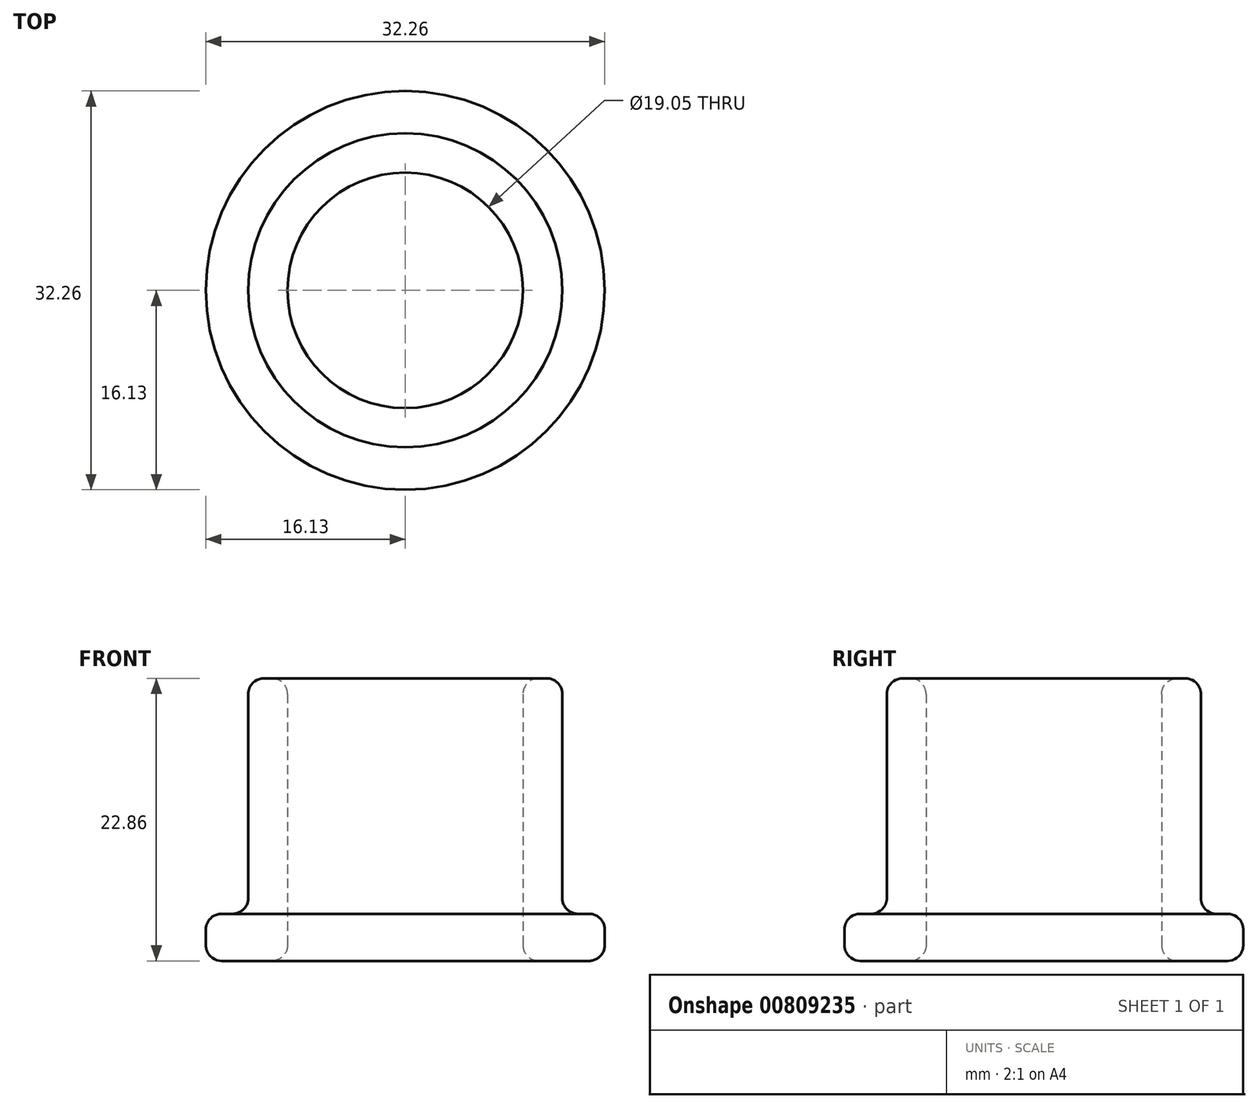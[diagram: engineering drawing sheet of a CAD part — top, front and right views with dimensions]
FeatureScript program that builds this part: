
annotation { "Feature Type Name" : "Feature", "Feature Type Description" : "" }
export const myFeature = defineFeature(function(context is Context, id is Id, definition is map)
    precondition{}
    {
        {
            var Q0;
            Q0=qCreatedBy(makeId("Front.planeOp"),FACE);
            var sketch = newSketch(context, id + "F0", { "sketchPlane" : qUnion([Q0])});
            skLineSegment(sketch, "E0", {"start": v(0, 0) * mm, "end": v(0, 26.62) * mm, "construction": true});
            skLineSegment(sketch, "E1", {"start": v(0, 0) * mm, "end": v(-16.13, 0) * mm, "construction": true});
            skLineSegment(sketch, "E2", {"start": v(-16.13, 0) * mm, "end": v(-16.13, 3.8) * mm});
            skLineSegment(sketch, "E3", {"start": v(-16.13, 3.8) * mm, "end": v(-12.7, 3.8) * mm});
            skLineSegment(sketch, "E4", {"start": v(-12.7, 3.8) * mm, "end": v(-12.7, 22.86) * mm});
            skLineSegment(sketch, "E5", {"start": v(-12.7, 22.86) * mm, "end": v(-9.53, 22.86) * mm});
            skLineSegment(sketch, "E6", {"start": v(-9.53, 22.86) * mm, "end": v(-9.53, 0) * mm});
            skLineSegment(sketch, "E7", {"start": v(-16.13, 0) * mm, "end": v(-9.53, 0) * mm});
            skSolve(sketch);
        }
        {
            var Q0;
            Q0=makeQuery(id+"F0.imprint","IMPRINT",FACE,{"disambiguationData":[TD([[makeQuery(id+"F0.imprint","IMPRINT",EDGE,{"derivedFrom":sQuery(id+"F0.wireOp",EDGE,"E2")}),-1.0]])]});
            var Q1;
            Q1=sQuery(id+"F0.wireOp",EDGE,"E0");
            revolve(context, id + "F1", {"surfaceOperationType" : NewSurfaceOperationType.NEW, "entities" : qUnion([Q0]), "axis" : qUnion([Q1]), "revolveType" : RevolveType.FULL});
        }
        {
            var Q0;
            Q0=makeQuery(id+"F1.opRevolve","SWEPT_EDGE",EDGE,{"disambiguationData":[OSD([sQuery(id+"F0.wireOp",EDGE,"E4"),sQuery(id+"F0.wireOp",EDGE,"E5")])]});
            var Q1;
            Q1=makeQuery(id+"F1.opRevolve","SWEPT_FACE",FACE,{"disambiguationData":[OSD([sQuery(id+"F0.wireOp",EDGE,"E5")])]});
            var Q2;
            Q2=makeQuery(id+"F1.opRevolve","SWEPT_EDGE",EDGE,{"disambiguationData":[OSD([sQuery(id+"F0.wireOp",EDGE,"E3"),sQuery(id+"F0.wireOp",EDGE,"E4")])]});
            var Q3;
            Q3=makeQuery(id+"F1.opRevolve","SWEPT_EDGE",EDGE,{"disambiguationData":[OSD([sQuery(id+"F0.wireOp",EDGE,"E2"),sQuery(id+"F0.wireOp",EDGE,"E3")])]});
            var Q4;
            Q4=makeQuery(id+"F1.opRevolve","SWEPT_EDGE",EDGE,{"disambiguationData":[OSD([sQuery(id+"F0.wireOp",EDGE,"E2"),sQuery(id+"F0.wireOp",EDGE,"E7")])]});
            var Q5;
            Q5=makeQuery(id+"F1.opRevolve","SWEPT_EDGE",EDGE,{"disambiguationData":[OSD([sQuery(id+"F0.wireOp",EDGE,"E6"),sQuery(id+"F0.wireOp",EDGE,"E7")])]});
            fillet(context, id + "F2", {"entities" : qUnion([Q0, Q1, Q2, Q3, Q4, Q5]), "radius" : 1.27 * mm, "tangentPropagation" : true, "allowEdgeOverflow" : false});
        }
    });
